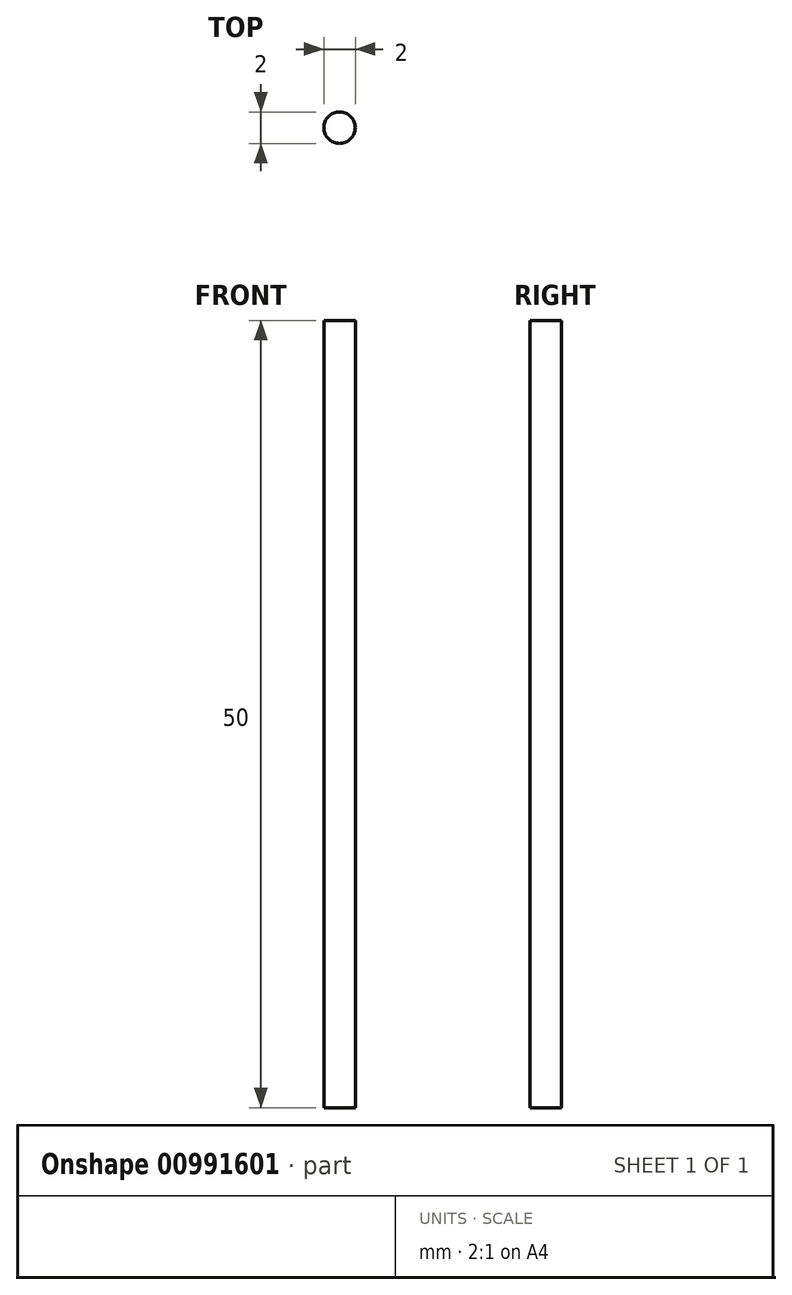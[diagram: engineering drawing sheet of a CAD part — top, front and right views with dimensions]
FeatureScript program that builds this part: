
annotation { "Feature Type Name" : "Feature", "Feature Type Description" : "" }
export const myFeature = defineFeature(function(context is Context, id is Id, definition is map)
    precondition{}
    {
        {
            var Q0;
            Q0=qCreatedBy(makeId("Top.planeOp"),FACE);
            var sketch = newSketch(context, id + "F0", { "sketchPlane" : qUnion([Q0])});
            skCircle(sketch, "E0", {"center": v(0, 0) * mm, "radius": 1 * mm});
            skSolve(sketch);
        }
        {
            var Q0;
            Q0=qSketchRegion(id+"F0",true);
            extrude(context, id + "F1", {"entities" : qUnion([Q0]), "depth" : 50 * mm, "offsetDistance" : 25 * mm});
        }
    });
